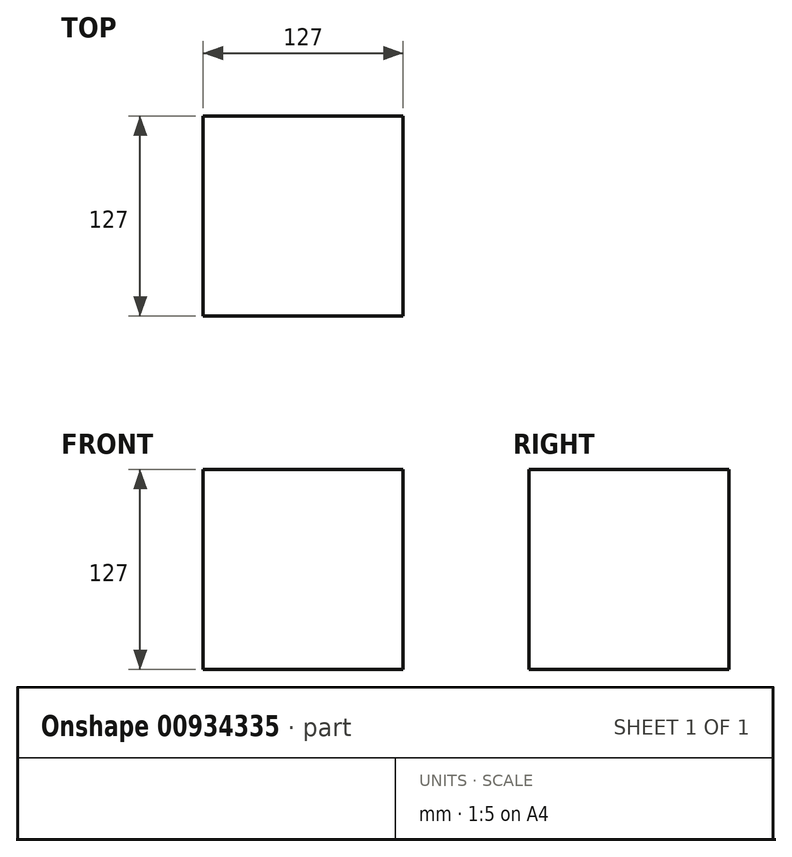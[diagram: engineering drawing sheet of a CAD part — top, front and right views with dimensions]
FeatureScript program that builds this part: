
annotation { "Feature Type Name" : "Feature", "Feature Type Description" : "" }
export const myFeature = defineFeature(function(context is Context, id is Id, definition is map)
    precondition{}
    {
        {
            var Q0;
            Q0=qCreatedBy(makeId("Front.planeOp"),FACE);
            var sketch = newSketch(context, id + "F0", { "sketchPlane" : qUnion([Q0])});
            skLineSegment(sketch, "E0.bottom", {"start": v(0, 0) * mm, "end": v(127, 0) * mm});
            skLineSegment(sketch, "E0.top", {"start": v(0, 127) * mm, "end": v(127, 127) * mm});
            skLineSegment(sketch, "E0.left", {"start": v(0, 0) * mm, "end": v(0, 127) * mm});
            skLineSegment(sketch, "E0.right", {"start": v(127, 0) * mm, "end": v(127, 127) * mm});
            skSolve(sketch);
        }
        {
            var Q0;
            Q0 = qSketchRegion(id + "F0", true);
            extrude(context, id + "F1", {"entities" : qUnion([Q0]), "depth" : 127 * mm, "offsetDistance" : 25.4 * mm});
        }
    });
